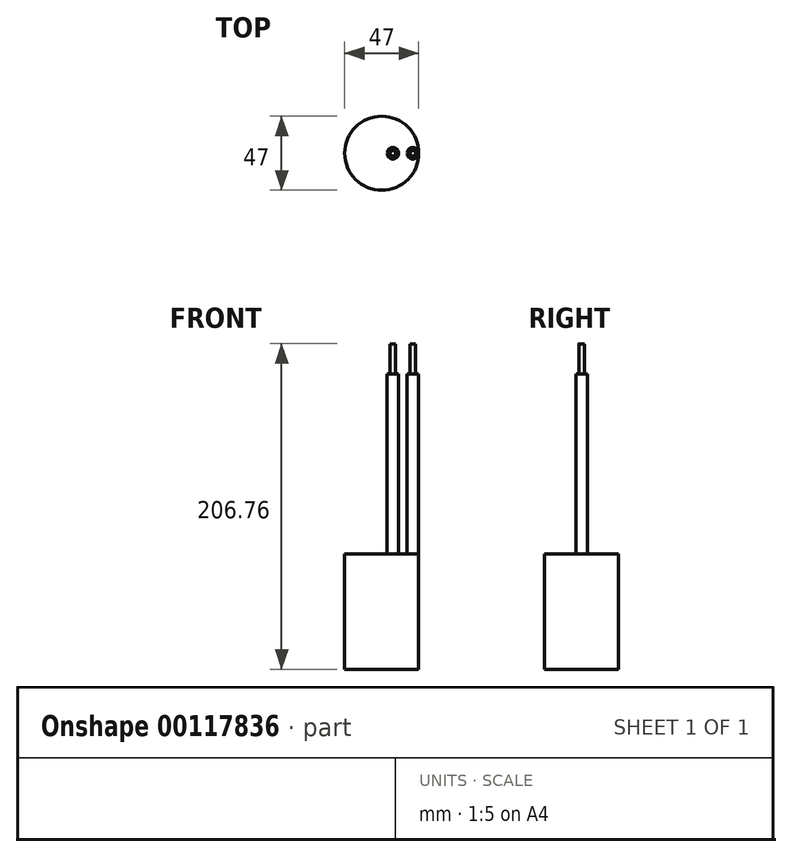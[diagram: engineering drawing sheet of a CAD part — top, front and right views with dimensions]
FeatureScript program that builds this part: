
annotation { "Feature Type Name" : "Feature", "Feature Type Description" : "" }
export const myFeature = defineFeature(function(context is Context, id is Id, definition is map)
    precondition{}
    {
        {
            var Q0;
            Q0=qCreatedBy(makeId("Top.planeOp"),FACE);
            var sketch = newSketch(context, id + "F0", { "sketchPlane" : qUnion([Q0])});
            skCircle(sketch, "E0", {"center": v(0, 0) * mm, "radius": 23.5 * mm});
            skSolve(sketch);
        }
        {
            var Q0;
            Q0 = qSketchRegion(id + "F0", true);
            extrude(context, id + "F1", {"entities" : qUnion([Q0]), "depth" : 73.15 * mm});
        }
        {
            var Q0;
            Q0=makeQuery(id+"F1.opExtrude","CAP_FACE",FACE,{"disambiguationData":[OSD([sQuery(id+"F0.wireOp",EDGE,"E0")])],"isStart":false});
            var sketch = newSketch(context, id + "F2", { "sketchPlane" : qUnion([Q0])});
            skCircle(sketch, "E1", {"center": v(19.81, 0) * mm, "radius": 3.62 * mm});
            skCircle(sketch, "E2", {"center": v(7.11, 0) * mm, "radius": 3.62 * mm});
            skSolve(sketch);
        }
        {
            var Q0;
            Q0 = qSketchRegion(id + "F2", true);
            extrude(context, id + "F3", {"entities" : qUnion([Q0]), "operationType" : NewBodyOperationType.ADD, "depth" : 114.55 * mm});
        }
        {
            var Q0;
            Q0=makeQuery(id+"F3.opExtrude","CAP_FACE",FACE,{"disambiguationData":[OSD([sQuery(id+"F2.wireOp",EDGE,"E1")])],"isStart":false});
            var sketch = newSketch(context, id + "F4", { "sketchPlane" : qUnion([Q0])});
            skCircle(sketch, "E3", {"center": v(7.11, 0) * mm, "radius": 1.78 * mm});
            skCircle(sketch, "E4", {"center": v(19.81, 0) * mm, "radius": 1.78 * mm});
            skSolve(sketch);
        }
        {
            var Q0;
            Q0 = qSketchRegion(id + "F4", true);
            extrude(context, id + "F5", {"entities" : qUnion([Q0]), "operationType" : NewBodyOperationType.ADD, "depth" : 19.05 * mm});
        }
    });
